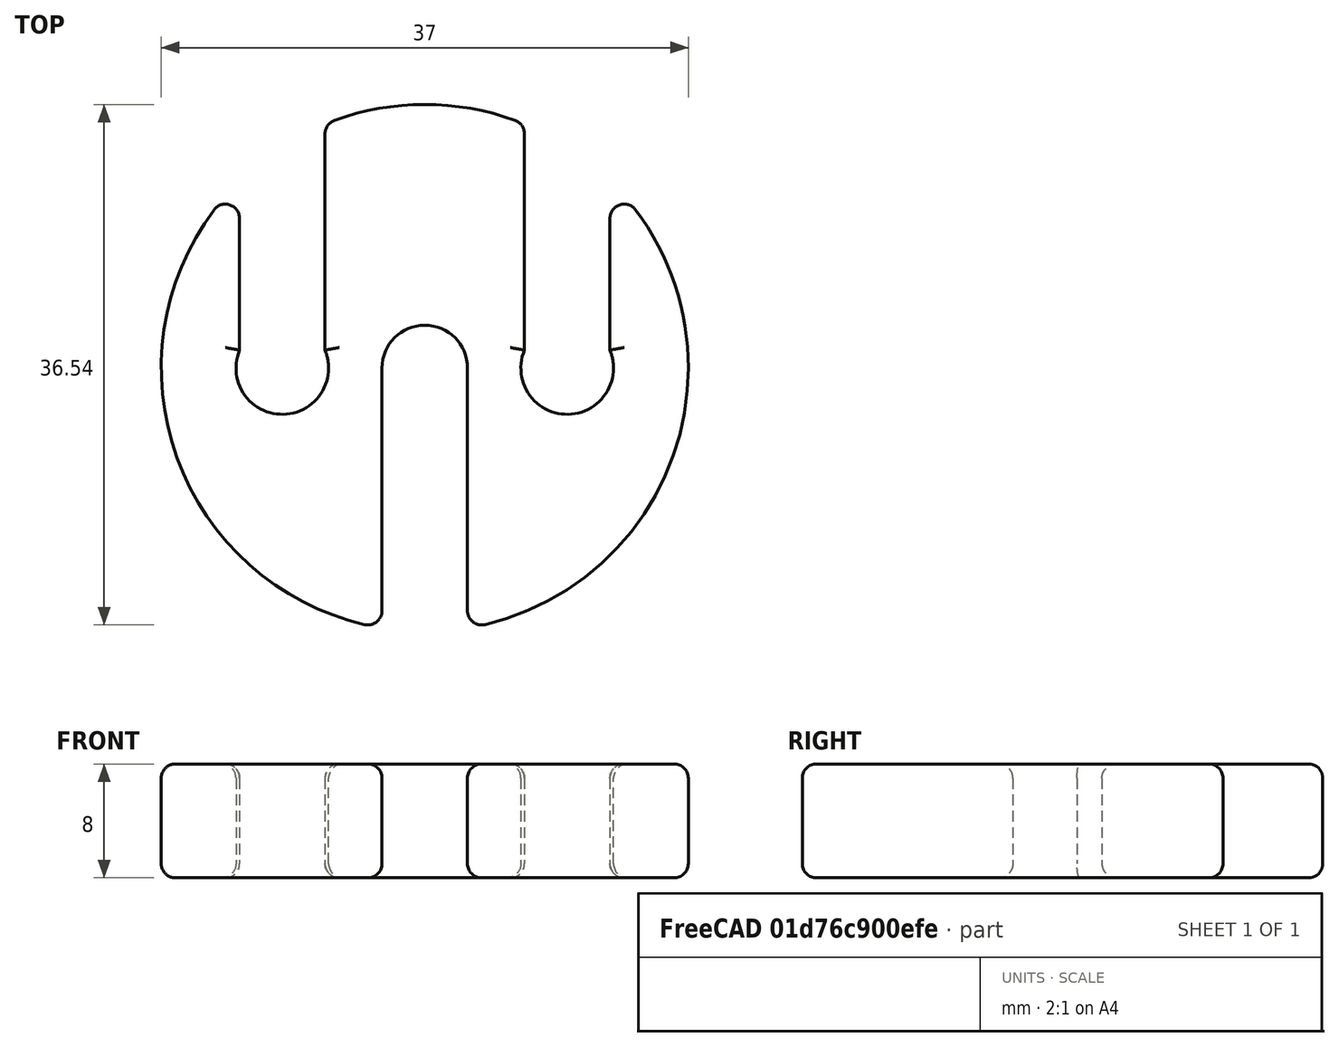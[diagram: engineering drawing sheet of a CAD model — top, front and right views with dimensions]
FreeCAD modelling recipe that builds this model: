
FCSTD DOCUMENT  (FreeCAD 1.0R1.0.0)
Label: Quak_Cryo_Pipe_Spacer
License: All rights reserved
LicenseURL: http://en.wikipedia.org/wiki/All_rights_reserved
objects: Part::Cylinder×5, Part::Box×3, Part::MultiFuse×1, Part::Cut×1, Part::Fillet×1
note: 11 computed .brp shape members not serialized (recipe doc carries the construction recipe); baked Part::Feature solids carry a one-line shape summary decoded from their .brp

FEATURE [Part::Cylinder] Cylinder
  Angle = 360
  AttacherType = Attacher::AttachEngine3D
  FirstAngle = 0
  Height = 8
  Radius = 18.5
  SecondAngle = 0
FEATURE [Part::Cylinder] Cylinder001
  Angle = 360
  AttacherType = Attacher::AttachEngine3D
  FirstAngle = 0
  Height = 10
  Placement = pos=(10,0,0) rot=(0,0,1;0rad)
  Radius = 3.25
  SecondAngle = 0
FEATURE [Part::Cylinder] Cylinder002
  Angle = 360
  AttacherType = Attacher::AttachEngine3D
  FirstAngle = 0
  Height = 10
  Placement = pos=(-10,0,0) rot=(0,0,1;0rad)
  Radius = 3.25
  SecondAngle = 0
FEATURE [Part::Box] Box  label="Cube"
  AttacherType = Attacher::AttachEngine3D
  Height = 10
  Length = 6
  Placement = pos=(7,0,0) rot=(0,0,1;0rad)
  Width = 20
FEATURE [Part::Box] Box001  label="Cube001"
  AttacherType = Attacher::AttachEngine3D
  Height = 10
  Length = 6
  Placement = pos=(-13,0,0) rot=(0,0,1;0rad)
  Width = 20
FEATURE [Part::Box] Box003  label="Cube003"
  AttacherType = Attacher::AttachEngine3D
  Height = 10
  Length = 6
  Placement = pos=(-3,-20,0) rot=(0,0,1;0rad)
  Width = 20
FEATURE [Part::Cylinder] Cylinder003
  Angle = 360
  AttacherType = Attacher::AttachEngine3D
  FirstAngle = 0
  Height = 10
  Placement = pos=(10,0,0) rot=(0,0,1;0rad)
  Radius = 3.25
  SecondAngle = 0
FEATURE [Part::Cylinder] Cylinder004
  Angle = 360
  AttacherType = Attacher::AttachEngine3D
  FirstAngle = 0
  Height = 10
  Radius = 3
  SecondAngle = 0
FEATURE [Part::MultiFuse] Fusion
  Shapes = -> [Cylinder004,Cylinder001,Cylinder002,Box,Box001,Box003,Cylinder003]
FEATURE [Part::Cut] Cut
  Base = -> Cylinder
  Tool = -> Fusion
FEATURE [Part::Fillet] Fillet
  Base = -> Cut
  EdgeLinks = -> Cut [Edge1,Edge2,Edge3,Edge5,Edge6,Edge7,Edge8,Edge9,Edge10,Edge11,Edge12,Edge13,Edge14,Edge15,Edge16,Edge17,Edge18,Edge19,Edge21,Edge22,Edge23,Edge24,Edge25,Edge26,Edge27,Edge28,Edge29,Edge30,Edge31,Edge32,Edge34,Edge37,Edge38,Edge42,Edge43]
  Edges = 35 edges r=1: [Edge1,Edge2,Edge3,Edge5,Edge6,Edge7,Edge8,Edge9,Edge10,Edge11,Edge12,Edge13,Edge14,Edge15,Edge16,Edge17,Edge18,Edge19,Edge21,Edge22,Edge23,Edge24,Edge25,Edge26,Edge27,Edge28,Edge29,Edge30,Edge31,Edge32,Edge34,Edge37,Edge38,Edge42,Edge43]
